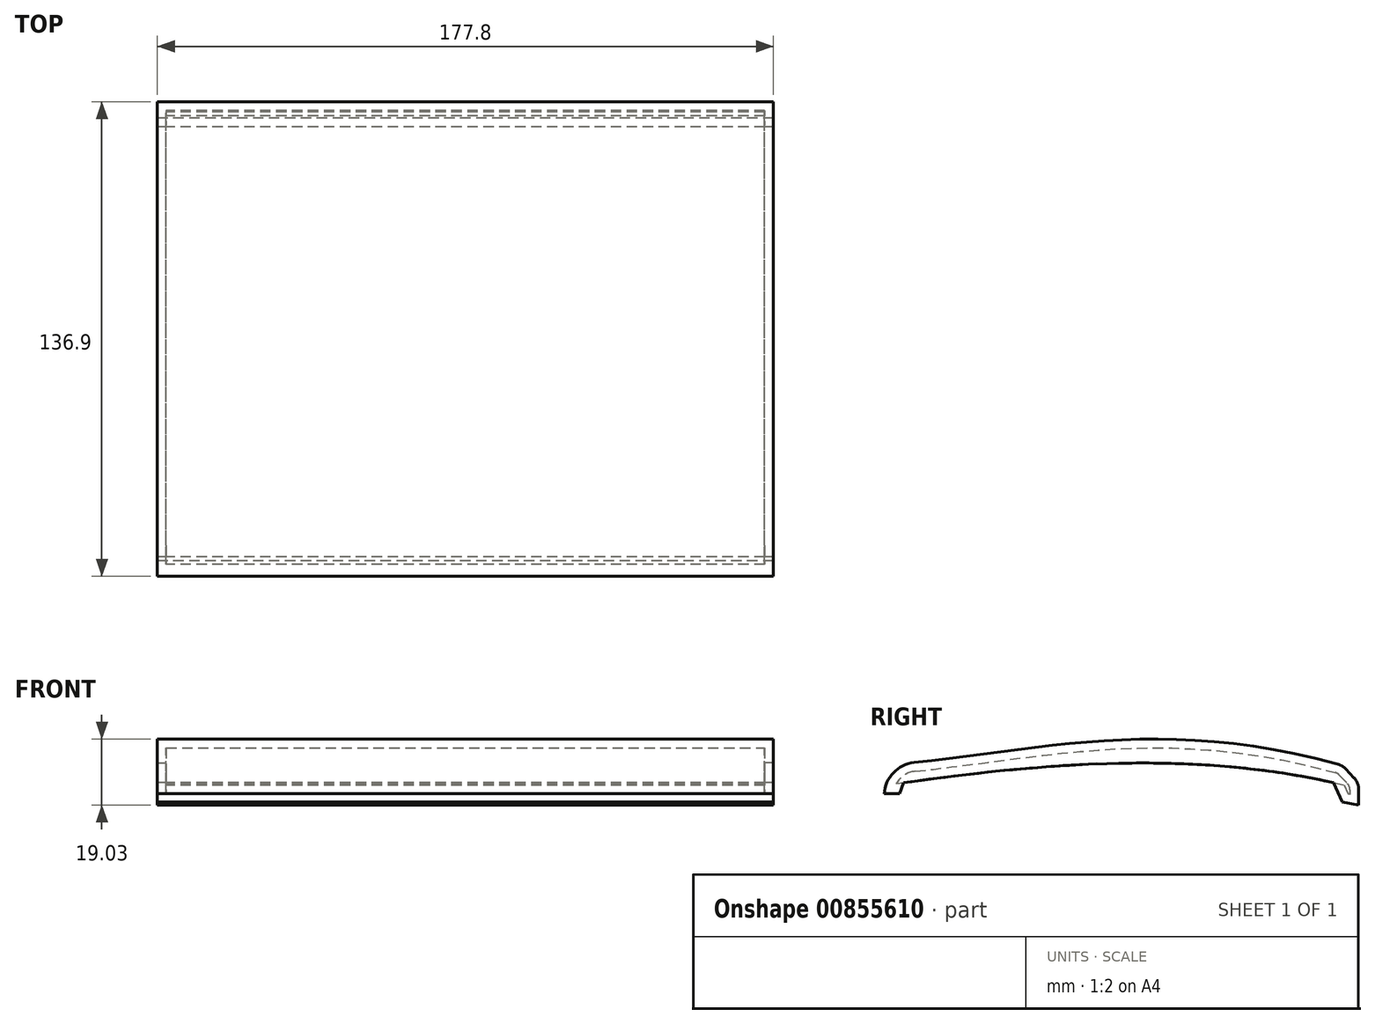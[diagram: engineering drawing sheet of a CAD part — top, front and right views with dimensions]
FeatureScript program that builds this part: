
annotation { "Feature Type Name" : "Feature", "Feature Type Description" : "" }
export const myFeature = defineFeature(function(context is Context, id is Id, definition is map)
    precondition{}
    {
        {
            var Q0;
            Q0=qCreatedBy(makeId("Right.planeOp"),FACE);
            var sketch = newSketch(context, id + "F0", { "sketchPlane" : qUnion([Q0])});
            skFitSpline(sketch, "E0", {"points": [v(-65.24, 0) * mm, v(58.86, 0) * mm], "startDerivative": vector(120.85, 16.67) * mm, "endDerivative": vector(125.69, -28.08) * mm});
            skLineSegment(sketch, "E1", {"start": v(-65.24, 0) * mm, "end": v(-66.39, -3.22) * mm});
            skLineSegment(sketch, "E2", {"start": v(-66.39, -3.22) * mm, "end": v(-70.8, -3.22) * mm});
            skLineSegment(sketch, "E3", {"start": v(-70.8, -3.22) * mm, "end": v(-70.8, 4.97) * mm});
            skFitSpline(sketch, "E4", {"points": [v(-70.8, 4.97) * mm, v(61.43, 4.97) * mm], "startDerivative": vector(129.97, 11.1) * mm, "endDerivative": vector(160.1, -45.33) * mm});
            skLineSegment(sketch, "E5", {"start": v(61.43, 4.97) * mm, "end": v(66.11, 0) * mm});
            skLineSegment(sketch, "E6", {"start": v(66.11, 0) * mm, "end": v(66.11, -6.44) * mm});
            skLineSegment(sketch, "E7", {"start": v(66.11, -6.44) * mm, "end": v(61.43, -5.56) * mm});
            skLineSegment(sketch, "E8", {"start": v(61.43, -5.56) * mm, "end": v(58.86, 0) * mm});
            skSolve(sketch);
        }
        {
            var Q0;
            Q0=makeQuery(id+"F0.imprint","IMPRINT",FACE,{"disambiguationData":[TD([[makeQuery(id+"F0.imprint","IMPRINT",EDGE,{"derivedFrom":sQuery(id+"F0.wireOp",EDGE,"E0")}),1.0]])]});
            extrude(context, id + "F1", {"entities" : qUnion([Q0]), "endBound" : BoundingType.SYMMETRIC, "depth" : 177.8 * mm, "offsetDistance" : 25.4 * mm});
        }
        {
            var Q0;
            Q0=makeQuery(id+"F1.opExtrude","SWEPT_EDGE",EDGE,{"disambiguationData":[OSD([sQuery(id+"F0.wireOp",EDGE,"E3"),sQuery(id+"F0.wireOp",EDGE,"E4")])]});
            fillet(context, id + "F2", {"entities" : qUnion([Q0]), "radius" : 9.65 * mm, "tangentPropagation" : true, "allowEdgeOverflow" : false});
        }
        {
            var Q0;
            Q0=makeQuery(id+"F1.opExtrude","SWEPT_EDGE",EDGE,{"disambiguationData":[OSD([sQuery(id+"F0.wireOp",EDGE,"E4"),sQuery(id+"F0.wireOp",EDGE,"E5")])]});
            fillet(context, id + "F3", {"entities" : qUnion([Q0]), "radius" : 5.08 * mm, "tangentPropagation" : true, "allowEdgeOverflow" : false});
        }
        {
            var Q0;
            Q0=makeQuery(id+"F1.opExtrude","SWEPT_EDGE",EDGE,{"disambiguationData":[OSD([sQuery(id+"F0.wireOp",EDGE,"E5"),sQuery(id+"F0.wireOp",EDGE,"E6")])]});
            fillet(context, id + "F4", {"entities" : qUnion([Q0]), "radius" : 5.08 * mm, "tangentPropagation" : true, "allowEdgeOverflow" : false});
        }
        {
            var Q0;
            Q0=makeQuery(id+"F1.opExtrude","SWEPT_FACE",FACE,{"disambiguationData":[OSD([sQuery(id+"F0.wireOp",EDGE,"E0")])]});
            shell(context, id + "F5", {"entities" : qUnion([Q0]), "thickness" : 2.54 * mm});
        }
    });
